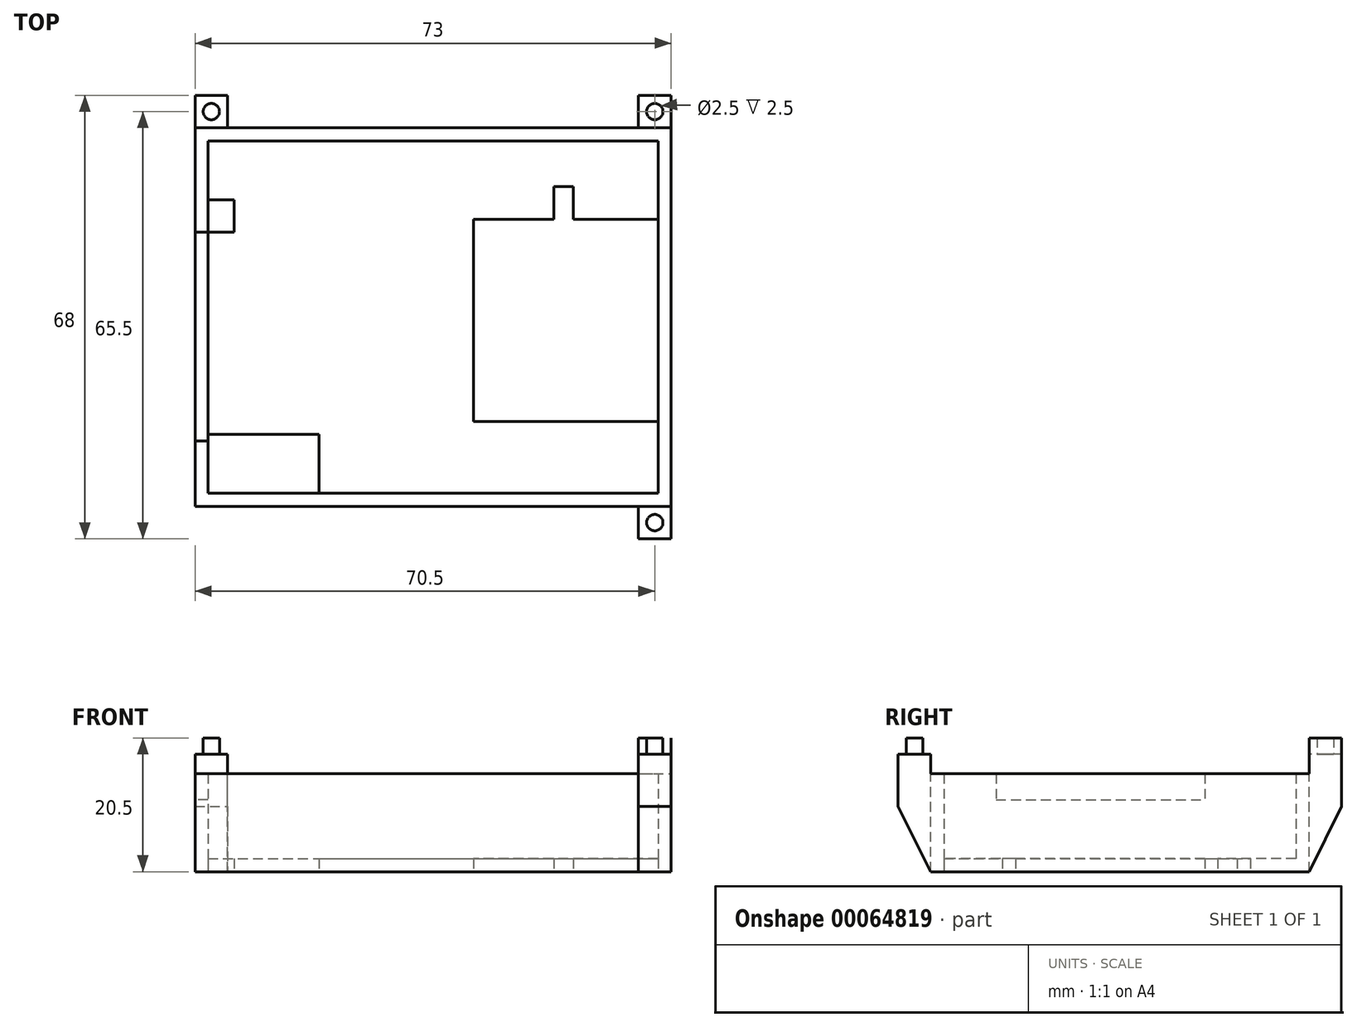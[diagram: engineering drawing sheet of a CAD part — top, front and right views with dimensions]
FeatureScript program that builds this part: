
annotation { "Feature Type Name" : "Feature", "Feature Type Description" : "" }
export const myFeature = defineFeature(function(context is Context, id is Id, definition is map)
    precondition{}
    {
        {
            var Q0;
            Q0=qCreatedBy(makeId("Top.planeOp"),FACE);
            var sketch = newSketch(context, id + "F0", { "sketchPlane" : qUnion([Q0])});
            skLineSegment(sketch, "E0.rect.bottom", {"start": v(-36.5, 29) * mm, "end": v(36.5, 29) * mm});
            skLineSegment(sketch, "E0.rect.top", {"start": v(-36.5, -29) * mm, "end": v(36.5, -29) * mm});
            skLineSegment(sketch, "E0.rect.left", {"start": v(-36.5, 29) * mm, "end": v(-36.5, -29) * mm});
            skLineSegment(sketch, "E0.rect.right", {"start": v(36.5, 29) * mm, "end": v(36.5, -29) * mm});
            skPoint(sketch, "E0.rect.middle", {"position": v(0, 0) * mm});
            skLineSegment(sketch, "E1.rect.bottom", {"start": v(-34.5, 27) * mm, "end": v(34.5, 27) * mm});
            skLineSegment(sketch, "E1.rect.top", {"start": v(-34.5, -27) * mm, "end": v(34.5, -27) * mm});
            skLineSegment(sketch, "E1.rect.left", {"start": v(-34.5, 27) * mm, "end": v(-34.5, -27) * mm});
            skLineSegment(sketch, "E1.rect.right", {"start": v(34.5, 27) * mm, "end": v(34.5, -27) * mm});
            skLineSegment(sketch, "E2.bottom", {"start": v(34.5, -16) * mm, "end": v(6.2, -16) * mm});
            skLineSegment(sketch, "E2.top", {"start": v(34.5, 15) * mm, "end": v(6.2, 15) * mm});
            skLineSegment(sketch, "E2.left", {"start": v(34.5, -16) * mm, "end": v(34.5, 15) * mm});
            skLineSegment(sketch, "E2.right", {"start": v(6.2, -16) * mm, "end": v(6.2, 15) * mm});
            skLineSegment(sketch, "E3.bottom", {"start": v(18.5, 15) * mm, "end": v(21.5, 15) * mm});
            skLineSegment(sketch, "E3.top", {"start": v(18.5, 20) * mm, "end": v(21.5, 20) * mm});
            skLineSegment(sketch, "E3.left", {"start": v(18.5, 15) * mm, "end": v(18.5, 20) * mm});
            skLineSegment(sketch, "E3.right", {"start": v(21.5, 15) * mm, "end": v(21.5, 20) * mm});
            skLineSegment(sketch, "E4.bottom", {"start": v(-34.5, -27) * mm, "end": v(-17.5, -27) * mm});
            skLineSegment(sketch, "E4.top", {"start": v(-34.5, -18) * mm, "end": v(-17.5, -18) * mm});
            skLineSegment(sketch, "E4.left", {"start": v(-34.5, -27) * mm, "end": v(-34.5, -18) * mm});
            skLineSegment(sketch, "E4.right", {"start": v(-17.5, -27) * mm, "end": v(-17.5, -18) * mm});
            skLineSegment(sketch, "E5.bottom", {"start": v(-34.5, 13) * mm, "end": v(-30.5, 13) * mm});
            skLineSegment(sketch, "E5.top", {"start": v(-34.5, 18) * mm, "end": v(-30.5, 18) * mm});
            skLineSegment(sketch, "E5.left", {"start": v(-34.5, 13) * mm, "end": v(-34.5, 18) * mm});
            skLineSegment(sketch, "E5.right", {"start": v(-30.5, 13) * mm, "end": v(-30.5, 18) * mm});
            skSolve(sketch);
        }
        {
            var Q0;
            Q0=makeQuery(id+"F0.imprint","IMPRINT",FACE,{"disambiguationData":[TD([[makeQuery(id+"F0.imprint","IMPRINT",EDGE,{"derivedFrom":sQuery(id+"F0.wireOp",EDGE,"E0.rect.bottom")}),-1.0]])]});
            extrude(context, id + "F1", {"entities" : qUnion([Q0]), "depth" : 15 * mm});
        }
        {
            var Q0;
            {var subQ9=sQuery(id+"F0.wireOp",EDGE,"E1.rect.bottom");Q0=makeQuery(id+"F0.imprint","IMPRINT",FACE,{"disambiguationData":[TD([[makeQuery(id+"F0.imprint","IMPRINT",EDGE,{"derivedFrom":subQ9}),-1.0]])]});}
            extrude(context, id + "F2", {"entities" : qUnion([Q0]), "operationType" : NewBodyOperationType.ADD, "depth" : 2 * mm});
        }
        {
            var Q0;
            Q0=makeQuery(id+"F1.opExtrude","SWEPT_FACE",FACE,{"disambiguationData":[OSD([sQuery(id+"F0.wireOp",EDGE,"E0.rect.bottom")])]});
            var sketch = newSketch(context, id + "F3", { "sketchPlane" : qUnion([Q0])});
            skLineSegment(sketch, "E6.bottom", {"start": v(-36.5, 0) * mm, "end": v(-31.5, 0) * mm});
            skLineSegment(sketch, "E6.top", {"start": v(-36.5, 15) * mm, "end": v(-31.5, 15) * mm});
            skLineSegment(sketch, "E6.left", {"start": v(-36.5, 0) * mm, "end": v(-36.5, 15) * mm});
            skLineSegment(sketch, "E6.right", {"start": v(-31.5, 0) * mm, "end": v(-31.5, 15) * mm});
            skLineSegment(sketch, "E7.bottom", {"start": v(36.5, 0) * mm, "end": v(31.5, 0) * mm});
            skLineSegment(sketch, "E7.top", {"start": v(36.5, 15) * mm, "end": v(31.5, 15) * mm});
            skLineSegment(sketch, "E7.left", {"start": v(36.5, 0) * mm, "end": v(36.5, 15) * mm});
            skLineSegment(sketch, "E7.right", {"start": v(31.5, 0) * mm, "end": v(31.5, 15) * mm});
            skSolve(sketch);
        }
        {
            var Q0;
            Q0=makeQuery(id+"F3.imprint","IMPRINT",FACE,{"disambiguationData":[TD([[makeQuery(id+"F3.imprint","IMPRINT",EDGE,{"derivedFrom":sQuery(id+"F3.wireOp",EDGE,"E6.bottom")}),-1.0]])]});
            var Q1;
            Q1=makeQuery(id+"F3.imprint","IMPRINT",FACE,{"disambiguationData":[TD([[makeQuery(id+"F3.imprint","IMPRINT",EDGE,{"derivedFrom":sQuery(id+"F3.wireOp",EDGE,"E7.bottom")}),-1.0]])]});
            extrude(context, id + "F4", {"entities" : qUnion([Q0, Q1]), "operationType" : NewBodyOperationType.ADD, "depth" : 5 * mm});
        }
        {
            var Q0;
            Q0=makeQuery(id+"F1.opExtrude","SWEPT_FACE",FACE,{"disambiguationData":[OSD([sQuery(id+"F0.wireOp",EDGE,"E0.rect.top")])]});
            var sketch = newSketch(context, id + "F5", { "sketchPlane" : qUnion([Q0])});
            skLineSegment(sketch, "E8.bottom", {"start": v(36.5, 0) * mm, "end": v(31.5, 0) * mm});
            skLineSegment(sketch, "E8.top", {"start": v(36.5, 15) * mm, "end": v(31.5, 15) * mm});
            skLineSegment(sketch, "E8.left", {"start": v(36.5, 0) * mm, "end": v(36.5, 15) * mm});
            skLineSegment(sketch, "E8.right", {"start": v(31.5, 0) * mm, "end": v(31.5, 15) * mm});
            skSolve(sketch);
        }
        {
            var Q0;
            Q0=makeQuery(id+"F5.imprint","IMPRINT",FACE,{"disambiguationData":[TD([[makeQuery(id+"F5.imprint","IMPRINT",EDGE,{"derivedFrom":sQuery(id+"F5.wireOp",EDGE,"E8.bottom")}),1.0]])]});
            extrude(context, id + "F6", {"entities" : qUnion([Q0]), "operationType" : NewBodyOperationType.ADD, "depth" : 5 * mm});
        }
        {
            var Q0;
            Q0=makeQuery(id+"F6.boolean.opBoolean","MERGE",FACE,{"derivedFrom":[makeQuery(id+"F4.boolean.opBoolean","MERGE",FACE,{"derivedFrom":[makeQuery(id+"F1.opExtrude","CAP_FACE",FACE,{"disambiguationData":[OSD([sQuery(id+"F0.wireOp",EDGE,"E0.rect.bottom"),sQuery(id+"F0.wireOp",EDGE,"E0.rect.top"),sQuery(id+"F0.wireOp",EDGE,"E0.rect.left"),sQuery(id+"F0.wireOp",EDGE,"E0.rect.right"),sQuery(id+"F0.wireOp",EDGE,"E1.rect.bottom"),sQuery(id+"F0.wireOp",EDGE,"E1.rect.top"),sQuery(id+"F0.wireOp",EDGE,"E1.rect.left"),sQuery(id+"F0.wireOp",EDGE,"E1.rect.right"),sQuery(id+"F0.wireOp",EDGE,"E2.left"),sQuery(id+"F0.wireOp",EDGE,"E4.bottom"),sQuery(id+"F0.wireOp",EDGE,"E4.left"),sQuery(id+"F0.wireOp",EDGE,"E5.left")])],"isStart":false}),makeQuery(id+"F4.opExtrude","SWEPT_FACE",FACE,{"disambiguationData":[OSD([sQuery(id+"F3.wireOp",EDGE,"E6.top")])]})]}),makeQuery(id+"F6.opExtrude","SWEPT_FACE",FACE,{"disambiguationData":[OSD([sQuery(id+"F5.wireOp",EDGE,"E8.top")])]})]});
            var sketch = newSketch(context, id + "F7", { "sketchPlane" : qUnion([Q0])});
            skCircle(sketch, "E9", {"center": v(34, -31.5) * mm, "radius": 1.25 * mm});
            skLineSegment(sketch, "E10", {"start": v(34.5, 0) * mm, "end": v(36.5, 0) * mm});
            skCircle(sketch, "E11.MirrorC", {"center": v(34, 31.5) * mm, "radius": 1.25 * mm});
            skLineSegment(sketch, "E12", {"start": v(0, 29) * mm, "end": v(0, 27) * mm});
            skCircle(sketch, "E13.MirrorC", {"center": v(-34, 31.5) * mm, "radius": 1.25 * mm});
            skLineSegment(sketch, "E14", {"start": v(31.5, -29) * mm, "end": v(36.5, -29) * mm});
            skLineSegment(sketch, "E15", {"start": v(31.5, 29) * mm, "end": v(36.5, 29) * mm});
            skLineSegment(sketch, "E16", {"start": v(-31.5, 29) * mm, "end": v(-36.5, 29) * mm});
            skSolve(sketch);
        }
        {
            var Q0;
            Q0=makeQuery(id+"F7.imprint","IMPRINT",FACE,{"disambiguationData":[TD([[makeQuery(id+"F7.imprint","IMPRINT",EDGE,{"derivedFrom":sQuery(id+"F7.wireOp",EDGE,"E9")}),1.0]])]});
            var Q1;
            Q1=makeQuery(id+"F7.imprint","IMPRINT",FACE,{"disambiguationData":[TD([[makeQuery(id+"F7.imprint","IMPRINT",EDGE,{"derivedFrom":sQuery(id+"F7.wireOp",EDGE,"E13.MirrorC")}),1.0]])]});
            extrude(context, id + "F8", {"entities" : qUnion([Q0, Q1]), "operationType" : NewBodyOperationType.ADD, "depth" : 5.5 * mm});
        }
        {
            var Q0;
            Q0=makeQuery(id+"F7.imprint","IMPRINT",FACE,{"disambiguationData":[TD([[makeQuery(id+"F7.imprint","IMPRINT",EDGE,{"derivedFrom":sQuery(id+"F7.wireOp",EDGE,"E11.MirrorC")}),-1.0]])]});
            extrude(context, id + "F9", {"entities" : qUnion([Q0]), "operationType" : NewBodyOperationType.ADD, "depth" : 5.5 * mm});
        }
        {
            var Q0;
            Q0=makeQuery(id+"F6.boolean.opBoolean","MERGE",FACE,{"derivedFrom":[makeQuery(id+"F4.boolean.opBoolean","MERGE",FACE,{"derivedFrom":[makeQuery(id+"F1.opExtrude","SWEPT_FACE",FACE,{"disambiguationData":[OSD([sQuery(id+"F0.wireOp",EDGE,"E0.rect.right")])]}),makeQuery(id+"F4.opExtrude","SWEPT_FACE",FACE,{"disambiguationData":[OSD([sQuery(id+"F3.wireOp",EDGE,"E6.left")])]})]}),makeQuery(id+"F6.opExtrude","SWEPT_FACE",FACE,{"disambiguationData":[OSD([sQuery(id+"F5.wireOp",EDGE,"E8.left")])]})]});
            var sketch = newSketch(context, id + "F10", { "sketchPlane" : qUnion([Q0])});
            skLineSegment(sketch, "E17", {"start": v(34, 10) * mm, "end": v(29, 0) * mm});
            skLineSegment(sketch, "E18", {"start": v(-34, 10) * mm, "end": v(-29, 0) * mm});
            skSolve(sketch);
        }
        {
            var Q0;
            {var subQ0=sQuery(id+"F10.wireOp",EDGE,"E18");Q0=makeQuery(id+"F10.imprint","IMPRINT",FACE,{"disambiguationData":[TD([[makeQuery(id+"F10.imprint","IMPRINT",EDGE,{"derivedFrom":subQ0}),-1.0]])]});}
            var Q1;
            {var subQ0=sQuery(id+"F10.wireOp",EDGE,"E17");Q1=makeQuery(id+"F10.imprint","IMPRINT",FACE,{"disambiguationData":[TD([[makeQuery(id+"F10.imprint","IMPRINT",EDGE,{"derivedFrom":subQ0}),1.0]])]});}
            extrude(context, id + "F11", {"entities" : qUnion([Q0, Q1]), "operationType" : NewBodyOperationType.REMOVE, "endBound" : BoundingType.THROUGH_ALL, "oppositeDirection" : true, "depth" : 25 * mm});
        }
        {
            var Q0;
            Q0=makeQuery(id+"F4.boolean.opBoolean","MERGE",FACE,{"derivedFrom":[makeQuery(id+"F1.opExtrude","SWEPT_FACE",FACE,{"disambiguationData":[OSD([sQuery(id+"F0.wireOp",EDGE,"E0.rect.left")])]}),makeQuery(id+"F4.opExtrude","SWEPT_FACE",FACE,{"disambiguationData":[OSD([sQuery(id+"F3.wireOp",EDGE,"E7.left")])]})]});
            var sketch = newSketch(context, id + "F12", { "sketchPlane" : qUnion([Q0])});
            skLineSegment(sketch, "E19.bottom", {"start": v(19, 15) * mm, "end": v(-13, 15) * mm});
            skLineSegment(sketch, "E19.top", {"start": v(19, 11) * mm, "end": v(-13, 11) * mm});
            skLineSegment(sketch, "E19.left", {"start": v(19, 15) * mm, "end": v(19, 11) * mm});
            skLineSegment(sketch, "E19.right", {"start": v(-13, 15) * mm, "end": v(-13, 11) * mm});
            skSolve(sketch);
        }
        {
            var Q0;
            Q0=makeQuery(id+"F12.imprint","IMPRINT",FACE,{"disambiguationData":[TD([[makeQuery(id+"F12.imprint","IMPRINT",EDGE,{"derivedFrom":sQuery(id+"F12.wireOp",EDGE,"E19.bottom")}),-1.0]])]});
            extrude(context, id + "F13", {"entities" : qUnion([Q0]), "operationType" : NewBodyOperationType.REMOVE, "oppositeDirection" : true, "depth" : 2 * mm});
        }
        {
            var Q0;
            Q0=makeQuery(id+"F7.imprint","IMPRINT",FACE,{"disambiguationData":[TD([[makeQuery(id+"F7.imprint","IMPRINT",EDGE,{"derivedFrom":sQuery(id+"F7.wireOp",EDGE,"E9")}),-1.0]])]});
            var Q1;
            Q1=makeQuery(id+"F7.imprint","IMPRINT",FACE,{"disambiguationData":[TD([[makeQuery(id+"F7.imprint","IMPRINT",EDGE,{"derivedFrom":sQuery(id+"F7.wireOp",EDGE,"E11.MirrorC")}),1.0]])]});
            var Q2;
            Q2=makeQuery(id+"F7.imprint","IMPRINT",FACE,{"disambiguationData":[TD([[makeQuery(id+"F7.imprint","IMPRINT",EDGE,{"derivedFrom":sQuery(id+"F7.wireOp",EDGE,"E13.MirrorC")}),-1.0]])]});
            extrude(context, id + "F14", {"entities" : qUnion([Q0, Q1, Q2]), "operationType" : NewBodyOperationType.ADD, "depth" : 3 * mm});
        }
    });
